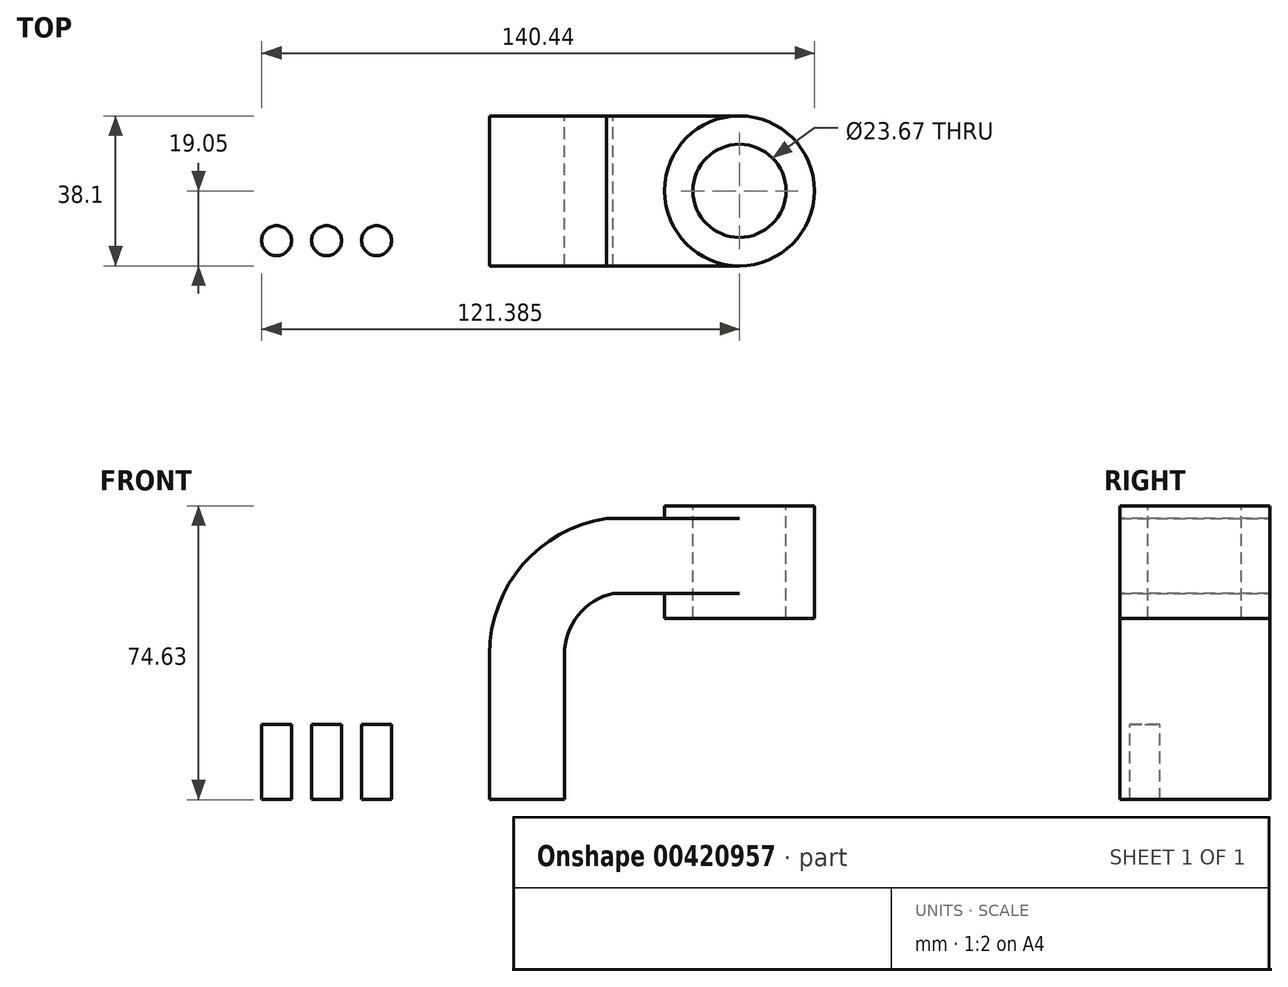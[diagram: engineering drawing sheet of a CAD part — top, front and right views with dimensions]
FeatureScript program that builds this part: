
annotation { "Feature Type Name" : "Feature", "Feature Type Description" : "" }
export const myFeature = defineFeature(function(context is Context, id is Id, definition is map)
    precondition{}
    {
        {
            var Q0;
            Q0=qCreatedBy(makeId("Front.planeOp"),FACE);
            var sketch = newSketch(context, id + "F0", { "sketchPlane" : qUnion([Q0])});
            skLineSegment(sketch, "E0.bottom", {"start": v(41.28, -9.52) * mm, "end": v(-41.28, -9.53) * mm});
            skLineSegment(sketch, "E0.top", {"start": v(41.28, 9.53) * mm, "end": v(-41.28, 9.52) * mm});
            skLineSegment(sketch, "E0.left", {"start": v(41.28, -9.52) * mm, "end": v(41.28, 9.53) * mm});
            skLineSegment(sketch, "E0.right", {"start": v(-41.28, -9.53) * mm, "end": v(-41.28, 9.52) * mm});
            skPoint(sketch, "E0.middle", {"position": v(0, 0) * mm});
            skLineSegment(sketch, "E1.bottom", {"start": v(111.12, 38.1) * mm, "end": v(60.32, 38.1) * mm});
            skLineSegment(sketch, "E1.top", {"start": v(111.12, 66.68) * mm, "end": v(60.32, 66.68) * mm});
            skLineSegment(sketch, "E1.left", {"start": v(111.12, 38.1) * mm, "end": v(111.12, 66.68) * mm});
            skLineSegment(sketch, "E1.right", {"start": v(60.32, 38.1) * mm, "end": v(60.32, 66.67) * mm});
            skPoint(sketch, "E1.middle", {"position": v(85.72, 52.39) * mm});
            skLineSegment(sketch, "E2", {"start": v(85.72, 66.68) * mm, "end": v(85.72, 38.1) * mm});
            skLineSegment(sketch, "E3", {"start": v(41.28, 9.53) * mm, "end": v(41.28, 27.4) * mm});
            skLineSegment(sketch, "E4", {"start": v(53.63, 42.88) * mm, "end": v(85.72, 42.88) * mm});
            skArc(sketch, "E5", {"start": v(41.27, 27.4) * mm, "mid": v(44.74, 37.3) * mm, "end": v(53.63, 42.88) * mm});
            skLineSegment(sketch, "E6.0", {"start": v(51.9, 61.93) * mm, "end": v(85.72, 61.93) * mm});
            skArc(sketch, "E6.1", {"start": v(22.22, 27.4) * mm, "mid": v(30.67, 50.16) * mm, "end": v(51.9, 61.93) * mm});
            skLineSegment(sketch, "E6.2", {"start": v(22.23, 9.53) * mm, "end": v(22.23, 27.4) * mm});
            skFitSpline(sketch, "E7", {"points": [v(-41.28, 9.52) * mm, v(51.9, 61.93) * mm], "startDerivative": vector(18.34, 86.84) * mm, "endDerivative": vector(181.65, 4.05) * mm});
            skSolve(sketch);
        }
        {
            var Q0;
            {var subQ4=sQuery(id+"F0.wireOp",EDGE,"E3");Q0=makeQuery(id+"F0.imprint","IMPRINT",FACE,{"disambiguationData":[TD([[makeQuery(id+"F0.imprint","IMPRINT",EDGE,{"derivedFrom":subQ4}),1.0]])]});}
            var Q1;
            Q1=makeQuery(id+"F0.imprint","IMPRINT",FACE,{"disambiguationData":[TD([[makeQuery(id+"F0.imprint","IMPRINT",EDGE,{"derivedFrom":sQuery(id+"F0.wireOp",EDGE,"E0.bottom")}),-1.0]])]});
            var Q2;
            {var subQ0=sQuery(id+"F0.wireOp",EDGE,"E4");var subQ1=sQuery(id+"F0.wireOp",EDGE,"E1.right");var subQ2=makeQuery(id+"F0.imprint","INTERSECT",VERTEX,{"derivedFrom":[subQ1,subQ0]});Q2=makeQuery(id+"F0.imprint","IMPRINT",FACE,{"disambiguationData":[TD([[makeQuery(id+"F0.imprint","IMPRINT",EDGE,{"disambiguationData":[TD([[subQ2,-1.0]])],"derivedFrom":subQ1}),-1.0]])]});}
            extrude(context, id + "F1", {"entities" : qUnion([Q0, Q1, Q2]), "endBound" : BoundingType.SYMMETRIC, "depth" : 38.1 * mm});
        }
        {
            var Q0;
            Q0=makeQuery(id+"F0.imprint","IMPRINT",FACE,{"disambiguationData":[TD([[makeQuery(id+"F0.imprint","IMPRINT",EDGE,{"derivedFrom":sQuery(id+"F0.wireOp",EDGE,"E6.1")}),1.0]])]});
            extrude(context, id + "F2", {"entities" : qUnion([Q0]), "operationType" : NewBodyOperationType.ADD, "endBound" : BoundingType.SYMMETRIC, "depth" : 12.7 * mm});
        }
        {
            var Q0;
            Q0=makeQuery(id+"F1.opExtrude","SWEPT_FACE",FACE,{"disambiguationData":[OSD([sQuery(id+"F0.wireOp",EDGE,"E6.0")])]});
            var sketch = newSketch(context, id + "F3", { "sketchPlane" : qUnion([Q0])});
            skCircle(sketch, "E8", {"center": v(85.72, 0) * mm, "radius": 19.05 * mm});
            skSolve(sketch);
        }
        {
            var Q0;
            {var subQ1=sQuery(id+"F0.wireOp",EDGE,"E6.0");var subQ2=makeQuery(id+"F1.opExtrude","SWEPT_EDGE",EDGE,{"disambiguationData":[OSD([sQuery(id+"F0.wireOp",EDGE,"E2"),subQ1])]});Q0=makeQuery(id+"F3.imprint","IMPRINT",FACE,{"disambiguationData":[TD([[makeQuery(id+"F3.imprint","IMPRINT",EDGE,{"derivedFrom":subQ2}),1.0]])]});}
            var Q1;
            {var subQ1=sQuery(id+"F0.wireOp",EDGE,"E6.0");var subQ2=makeQuery(id+"F1.opExtrude","SWEPT_EDGE",EDGE,{"disambiguationData":[OSD([sQuery(id+"F0.wireOp",EDGE,"E2"),subQ1])]});Q1=makeQuery(id+"F3.imprint","IMPRINT",FACE,{"disambiguationData":[TD([[makeQuery(id+"F3.imprint","IMPRINT",EDGE,{"derivedFrom":subQ2}),-1.0]])]});}
            extrude(context, id + "F4", {"entities" : qUnion([Q0, Q1]), "operationType" : NewBodyOperationType.ADD, "depth" : 3.17 * mm, "hasSecondDirection" : true, "secondDirectionOppositeDirection" : true, "secondDirectionDepth" : 25.4 * mm});
        }
        {
            var Q0;
            Q0=makeQuery(id+"F4.opExtrude","CAP_FACE",FACE,{"disambiguationData":[OSD([sQuery(id+"F3.wireOp",EDGE,"E8")])],"isStart":false});
            var sketch = newSketch(context, id + "F5", { "sketchPlane" : qUnion([Q0])});
            skCircle(sketch, "E9", {"center": v(85.72, 0) * mm, "radius": 11.84 * mm});
            skSolve(sketch);
        }
        {
            var Q0;
            Q0=makeQuery(id+"F5.imprint","IMPRINT",FACE,{"disambiguationData":[TD([[makeQuery(id+"F5.imprint","IMPRINT",EDGE,{"derivedFrom":sQuery(id+"F5.wireOp",EDGE,"E9")}),1.0]])]});
            extrude(context, id + "F6", {"entities" : qUnion([Q0]), "operationType" : NewBodyOperationType.REMOVE, "oppositeDirection" : true, "depth" : 50.8 * mm});
        }
        {
            var Q0;
            {var subQ0=sQuery(id+"F0.wireOp",EDGE,"E7");var subQ1=sQuery(id+"F0.wireOp",EDGE,"E6.2");var subQ2=sQuery(id+"F0.wireOp",EDGE,"E6.1");var subQ3=sQuery(id+"F0.wireOp",EDGE,"E0.top");Q0=makeQuery(id+"F2.boolean.opBoolean","SPLIT",FACE,{"disambiguationData":[TD([makeQuery(id+"F2.opExtrude","CAP_FACE",FACE,{"disambiguationData":[OSD([subQ3,subQ2,subQ1,subQ0])],"isStart":true})])],"derivedFrom":makeQuery(id+"F1.opExtrude","SWEPT_FACE",FACE,{"disambiguationData":[OSD([subQ3])]})});}
            var sketch = newSketch(context, id + "F7", { "sketchPlane" : qUnion([Q0])});
            skCircle(sketch, "E10", {"center": v(-31.85, 12.65) * mm, "radius": 3.81 * mm});
            skCircle(sketch, "E11.1.0.0", {"center": v(-19.15, 12.65) * mm, "radius": 3.81 * mm});
            skCircle(sketch, "E11.2.0.0", {"center": v(-6.45, 12.65) * mm, "radius": 3.81 * mm});
            skLineSegment(sketch, "E11.direction1", {"start": v(-31.85, 12.65) * mm, "end": v(-19.15, 12.65) * mm, "construction": true});
            skCircle(sketch, "E12.MirrorC", {"center": v(-31.85, -12.65) * mm, "radius": 3.81 * mm});
            skCircle(sketch, "E13.MirrorC", {"center": v(-19.15, -12.65) * mm, "radius": 3.81 * mm});
            skCircle(sketch, "E14.MirrorC", {"center": v(-6.45, -12.65) * mm, "radius": 3.81 * mm});
            skSolve(sketch);
        }
        {
            var Q0;
            Q0=makeQuery(id+"F7.imprint","IMPRINT",FACE,{"disambiguationData":[TD([[makeQuery(id+"F7.imprint","IMPRINT",EDGE,{"derivedFrom":sQuery(id+"F7.wireOp",EDGE,"E14.MirrorC")}),-1.0]])]});
            var Q1;
            Q1=makeQuery(id+"F7.imprint","IMPRINT",FACE,{"disambiguationData":[TD([[makeQuery(id+"F7.imprint","IMPRINT",EDGE,{"derivedFrom":sQuery(id+"F7.wireOp",EDGE,"E13.MirrorC")}),-1.0]])]});
            var Q2;
            Q2=makeQuery(id+"F7.imprint","IMPRINT",FACE,{"disambiguationData":[TD([[makeQuery(id+"F7.imprint","IMPRINT",EDGE,{"derivedFrom":sQuery(id+"F7.wireOp",EDGE,"E12.MirrorC")}),-1.0]])]});
            var Q3;
            Q3=makeQuery(id+"F7.imprint","IMPRINT",FACE,{"disambiguationData":[TD([[makeQuery(id+"F7.imprint","IMPRINT",EDGE,{"derivedFrom":sQuery(id+"F7.wireOp",EDGE,"E11.2.0.0")}),1.0]])]});
            var Q4;
            Q4=makeQuery(id+"F7.imprint","IMPRINT",FACE,{"disambiguationData":[TD([[makeQuery(id+"F7.imprint","IMPRINT",EDGE,{"derivedFrom":sQuery(id+"F7.wireOp",EDGE,"E11.1.0.0")}),1.0]])]});
            var Q5;
            Q5=makeQuery(id+"F7.imprint","IMPRINT",FACE,{"disambiguationData":[TD([[makeQuery(id+"F7.imprint","IMPRINT",EDGE,{"derivedFrom":sQuery(id+"F7.wireOp",EDGE,"E10")}),1.0]])]});
            extrude(context, id + "F8", {"entities" : qUnion([Q0, Q1, Q2, Q3, Q4, Q5]), "operationType" : NewBodyOperationType.REMOVE, "oppositeDirection" : true, "depth" : 25.4 * mm});
        }
    });
